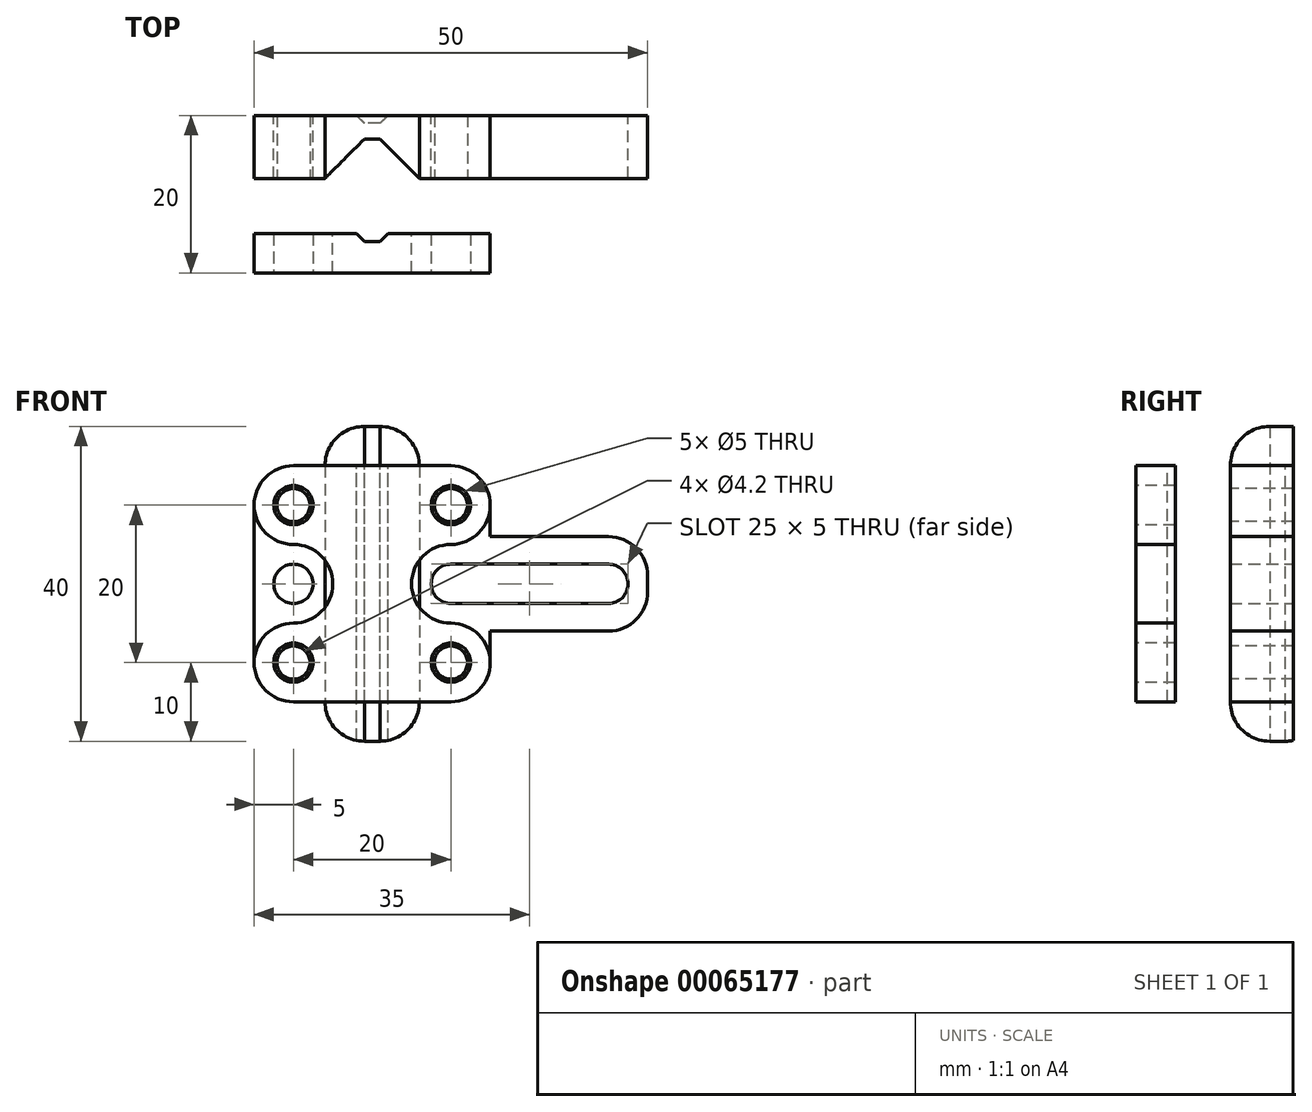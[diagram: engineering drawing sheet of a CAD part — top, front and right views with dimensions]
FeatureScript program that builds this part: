
annotation { "Feature Type Name" : "Feature", "Feature Type Description" : "" }
export const myFeature = defineFeature(function(context is Context, id is Id, definition is map)
    precondition{}
    {
        {
            var Q0;
            Q0=qCreatedBy(makeId("Front.planeOp"),FACE);
            var sketch = newSketch(context, id + "F0", { "sketchPlane" : qUnion([Q0])});
            skCircle(sketch, "E0", {"center": v(0, 0) * mm, "radius": 2.5 * mm, "construction": true});
            skCircle(sketch, "E1.0.1.0", {"center": v(0, 10) * mm, "radius": 2.5 * mm, "construction": true});
            skCircle(sketch, "E1.0.2.0", {"center": v(0, 20) * mm, "radius": 2.5 * mm, "construction": true});
            skCircle(sketch, "E1.0.3.0", {"center": v(0, 30) * mm, "radius": 2.5 * mm, "construction": true});
            skCircle(sketch, "E1.0.4.0", {"center": v(0, 40) * mm, "radius": 2.5 * mm, "construction": true});
            skCircle(sketch, "E1.1.0.0", {"center": v(10, 0) * mm, "radius": 2.5 * mm, "construction": true});
            skCircle(sketch, "E1.1.1.0", {"center": v(10, 10) * mm, "radius": 2.5 * mm, "construction": true});
            skCircle(sketch, "E1.1.2.0", {"center": v(10, 20) * mm, "radius": 2.5 * mm, "construction": true});
            skCircle(sketch, "E1.1.3.0", {"center": v(10, 30) * mm, "radius": 2.5 * mm, "construction": true});
            skCircle(sketch, "E1.1.4.0", {"center": v(10, 40) * mm, "radius": 2.5 * mm, "construction": true});
            skCircle(sketch, "E1.2.0.0", {"center": v(20, 0) * mm, "radius": 2.5 * mm, "construction": true});
            skCircle(sketch, "E1.2.1.0", {"center": v(20, 10) * mm, "radius": 2.1 * mm, "construction": true});
            skCircle(sketch, "E1.2.2.0", {"center": v(20, 20) * mm, "radius": 2.5 * mm});
            skCircle(sketch, "E1.2.3.0", {"center": v(20, 30) * mm, "radius": 2.1 * mm, "construction": true});
            skCircle(sketch, "E1.2.4.0", {"center": v(20, 40) * mm, "radius": 2.5 * mm, "construction": true});
            skCircle(sketch, "E1.3.0.0", {"center": v(30, 0) * mm, "radius": 2.5 * mm, "construction": true});
            skCircle(sketch, "E1.3.1.0", {"center": v(30, 10) * mm, "radius": 2.5 * mm, "construction": true});
            skCircle(sketch, "E1.3.2.0", {"center": v(30, 20) * mm, "radius": 2.5 * mm, "construction": true});
            skCircle(sketch, "E1.3.3.0", {"center": v(30, 30) * mm, "radius": 2.5 * mm, "construction": true});
            skCircle(sketch, "E1.3.4.0", {"center": v(30, 40) * mm, "radius": 2.5 * mm, "construction": true});
            skCircle(sketch, "E1.4.0.0", {"center": v(40, 0) * mm, "radius": 2.5 * mm, "construction": true});
            skCircle(sketch, "E1.4.1.0", {"center": v(40, 10) * mm, "radius": 2.1 * mm, "construction": true});
            skArc(sketch, "E1.4.2.0", {"start": v(40, 22.5) * mm, "mid": v(37.5, 20) * mm, "end": v(40, 17.5) * mm});
            skCircle(sketch, "E1.4.3.0", {"center": v(40, 30) * mm, "radius": 2.1 * mm, "construction": true});
            skCircle(sketch, "E1.4.4.0", {"center": v(40, 40) * mm, "radius": 2.5 * mm, "construction": true});
            skCircle(sketch, "E1.5.0.0", {"center": v(50, 0) * mm, "radius": 2.5 * mm, "construction": true});
            skCircle(sketch, "E1.5.1.0", {"center": v(50, 10) * mm, "radius": 2.5 * mm, "construction": true});
            skCircle(sketch, "E1.5.3.0", {"center": v(50, 30) * mm, "radius": 2.5 * mm, "construction": true});
            skCircle(sketch, "E1.5.4.0", {"center": v(50, 40) * mm, "radius": 2.5 * mm, "construction": true});
            skCircle(sketch, "E1.6.0.0", {"center": v(60, 0) * mm, "radius": 2.5 * mm, "construction": true});
            skCircle(sketch, "E1.6.1.0", {"center": v(60, 10) * mm, "radius": 2.5 * mm, "construction": true});
            skArc(sketch, "E1.6.2.0", {"start": v(60, 17.5) * mm, "mid": v(62.5, 20) * mm, "end": v(60, 22.5) * mm});
            skCircle(sketch, "E1.6.3.0", {"center": v(60, 30) * mm, "radius": 2.5 * mm, "construction": true});
            skCircle(sketch, "E1.6.4.0", {"center": v(60, 40) * mm, "radius": 2.5 * mm, "construction": true});
            skCircle(sketch, "E1.7.0.0", {"center": v(70, 0) * mm, "radius": 2.5 * mm, "construction": true});
            skCircle(sketch, "E1.7.1.0", {"center": v(70, 10) * mm, "radius": 2.5 * mm, "construction": true});
            skCircle(sketch, "E1.7.2.0", {"center": v(70, 20) * mm, "radius": 2.5 * mm, "construction": true});
            skCircle(sketch, "E1.7.3.0", {"center": v(70, 30) * mm, "radius": 2.5 * mm, "construction": true});
            skCircle(sketch, "E1.7.4.0", {"center": v(70, 40) * mm, "radius": 2.5 * mm, "construction": true});
            skCircle(sketch, "E1.8.0.0", {"center": v(80, 0) * mm, "radius": 2.5 * mm, "construction": true});
            skCircle(sketch, "E1.8.1.0", {"center": v(80, 10) * mm, "radius": 2.5 * mm, "construction": true});
            skCircle(sketch, "E1.8.2.0", {"center": v(80, 20) * mm, "radius": 2.5 * mm, "construction": true});
            skCircle(sketch, "E1.8.3.0", {"center": v(80, 30) * mm, "radius": 2.5 * mm, "construction": true});
            skCircle(sketch, "E1.8.4.0", {"center": v(80, 40) * mm, "radius": 2.5 * mm, "construction": true});
            skLineSegment(sketch, "E1.direction1", {"start": v(0, 0) * mm, "end": v(10, 0) * mm, "construction": true});
            skLineSegment(sketch, "E1.direction2", {"start": v(0, 0) * mm, "end": v(0, 10) * mm, "construction": true});
            skLineSegment(sketch, "E2.bottom", {"start": v(36, 0) * mm, "end": v(24, 0) * mm});
            skLineSegment(sketch, "E2.top", {"start": v(36, 40) * mm, "end": v(24, 40) * mm});
            skLineSegment(sketch, "E2.left", {"start": v(36, 0) * mm, "end": v(36, 5) * mm});
            skLineSegment(sketch, "E2.right", {"start": v(24, 0) * mm, "end": v(24, 5) * mm});
            skLineSegment(sketch, "E3.bottom", {"start": v(65, 14) * mm, "end": v(45, 14) * mm});
            skLineSegment(sketch, "E3.top", {"start": v(65, 26) * mm, "end": v(45, 26) * mm});
            skLineSegment(sketch, "E3.left", {"start": v(65, 14) * mm, "end": v(65, 26) * mm});
            skLineSegment(sketch, "E3.right", {"start": v(15, 14) * mm, "end": v(15, 26) * mm});
            skLineSegment(sketch, "E4.trimOffspring", {"start": v(24, 35) * mm, "end": v(24, 40) * mm});
            skLineSegment(sketch, "E5.trimOffspring", {"start": v(36, 35) * mm, "end": v(36, 40) * mm});
            skLineSegment(sketch, "E6", {"start": v(40, 22.5) * mm, "end": v(60, 22.5) * mm});
            skLineSegment(sketch, "E7", {"start": v(60, 17.5) * mm, "end": v(40, 17.5) * mm});
            skLineSegment(sketch, "E8", {"start": v(15, 26) * mm, "end": v(15, 35) * mm});
            skLineSegment(sketch, "E9", {"start": v(15, 35) * mm, "end": v(24, 35) * mm});
            skLineSegment(sketch, "E10", {"start": v(45, 35) * mm, "end": v(45, 26) * mm});
            skLineSegment(sketch, "E11", {"start": v(45, 5) * mm, "end": v(36, 5) * mm});
            skLineSegment(sketch, "E12", {"start": v(15, 5) * mm, "end": v(15, 14) * mm});
            skLineSegment(sketch, "E13.trimOffspring", {"start": v(36, 35) * mm, "end": v(45, 35) * mm});
            skLineSegment(sketch, "E14.trimOffspring", {"start": v(24, 5) * mm, "end": v(15, 5) * mm});
            skLineSegment(sketch, "E15.trimOffspring", {"start": v(45, 14) * mm, "end": v(45, 5) * mm});
            skSolve(sketch);
        }
        {
            var Q0;
            Q0=makeQuery(id+"F0.imprint","IMPRINT",FACE,{"disambiguationData":[TD([[makeQuery(id+"F0.imprint","IMPRINT",EDGE,{"derivedFrom":sQuery(id+"F0.wireOp",EDGE,"E1.2.1.0")}),-1.0]])]});
            var Q1;
            Q1=makeQuery(id+"F0.imprint","IMPRINT",FACE,{"disambiguationData":[TD([[makeQuery(id+"F0.imprint","IMPRINT",EDGE,{"derivedFrom":sQuery(id+"F0.wireOp",EDGE,"E1.2.2.0")}),-1.0]])]});
            extrude(context, id + "F1", {"entities" : qUnion([Q0, Q1]), "depth" : 8 * mm});
        }
        {
            var Q0;
            Q0=qCreatedBy(makeId("Top.planeOp"),FACE);
            var sketch = newSketch(context, id + "F2", { "sketchPlane" : qUnion([Q0])});
            skLineSegment(sketch, "E16", {"start": v(24, -8) * mm, "end": v(29, -3) * mm});
            skLineSegment(sketch, "E17", {"start": v(29, -3) * mm, "end": v(31, -3) * mm});
            skLineSegment(sketch, "E18", {"start": v(31, -3) * mm, "end": v(36, -8) * mm});
            skLineSegment(sketch, "E19", {"start": v(36, -8) * mm, "end": v(24, -8) * mm});
            skSolve(sketch);
        }
        {
            var Q0;
            Q0=makeQuery(id+"F2.imprint","IMPRINT",FACE,{"disambiguationData":[TD([[makeQuery(id+"F2.imprint","IMPRINT",EDGE,{"derivedFrom":sQuery(id+"F2.wireOp",EDGE,"E16")}),-1.0]])]});
            extrude(context, id + "F3", {"entities" : qUnion([Q0]), "operationType" : NewBodyOperationType.REMOVE, "depth" : 40 * mm});
        }
        {
            var Q0;
            Q0=sQuery(id+"F0.wireOp",VERTEX,"E1.2.3.0.center");
            var Q1;
            Q1=sQuery(id+"F0.wireOp",VERTEX,"E1.4.3.0.center");
            var Q2;
            Q2=sQuery(id+"F0.wireOp",VERTEX,"E1.4.1.0.center");
            var Q3;
            Q3=sQuery(id+"F0.wireOp",VERTEX,"E1.2.1.0.center");
            var Q4;
            Q4=makeQuery(id+"F1.opExtrude","SWEPT_BODY",BODY,{"disambiguationData":[OSD([sQuery(id+"F0.wireOp",EDGE,"E1.2.1.0"),sQuery(id+"F0.wireOp",EDGE,"E1.2.2.0"),sQuery(id+"F0.wireOp",EDGE,"E1.2.3.0"),sQuery(id+"F0.wireOp",EDGE,"E1.4.1.0"),sQuery(id+"F0.wireOp",EDGE,"E1.4.2.0"),sQuery(id+"F0.wireOp",EDGE,"E1.4.3.0"),sQuery(id+"F0.wireOp",EDGE,"E1.6.2.0"),sQuery(id+"F0.wireOp",EDGE,"E2.bottom"),sQuery(id+"F0.wireOp",EDGE,"E2.top"),sQuery(id+"F0.wireOp",EDGE,"E2.left"),sQuery(id+"F0.wireOp",EDGE,"E2.right"),sQuery(id+"F0.wireOp",EDGE,"E3.bottom"),sQuery(id+"F0.wireOp",EDGE,"E3.top"),sQuery(id+"F0.wireOp",EDGE,"E3.left"),sQuery(id+"F0.wireOp",EDGE,"E3.right"),sQuery(id+"F0.wireOp",EDGE,"E4.trimOffspring"),sQuery(id+"F0.wireOp",EDGE,"E5.trimOffspring"),sQuery(id+"F0.wireOp",EDGE,"E6"),sQuery(id+"F0.wireOp",EDGE,"E7"),sQuery(id+"F0.wireOp",EDGE,"E8"),sQuery(id+"F0.wireOp",EDGE,"E9"),sQuery(id+"F0.wireOp",EDGE,"E10"),sQuery(id+"F0.wireOp",EDGE,"E11"),sQuery(id+"F0.wireOp",EDGE,"E12"),sQuery(id+"F0.wireOp",EDGE,"E13.trimOffspring"),sQuery(id+"F0.wireOp",EDGE,"E14.trimOffspring"),sQuery(id+"F0.wireOp",EDGE,"E15.trimOffspring")])]});
            hole(context, id + "F4", {"style" : HoleStyle.SIMPLE, "endStyle" : HoleEndStyle.THROUGH, "oppositeDirection" : true, "standardTappedOrClearance" : lookupTablePath({ "standard" : "ISO", "engagement" : "75%", "pitch" : "0.8 mm", "size" : "M5", "type" : "Tapped" }), "standardBlindInLast" : lookupTablePath({ "standard" : "ISO", "engagement" : "75%", "pitch" : "0.8 mm", "size" : "M5", "type" : "Tapped" }), "holeDiameter" : 4.2 * mm, "showTappedDepth" : true, "isTappedThrough" : true, "tappedDepth" : 12 * mm, "tapClearance" : 3, "locations" : qUnion([Q0, Q1, Q2, Q3]), "scope" : qUnion([Q4]), "majorDiameter" : 5 * mm, "startStyle" : HoleStartStyle.PART});
        }
        {
            var Q0;
            Q0=makeQuery(id+"F1.opExtrude","SWEPT_EDGE",EDGE,{"disambiguationData":[OSD([sQuery(id+"F0.wireOp",EDGE,"E2.top"),sQuery(id+"F0.wireOp",EDGE,"E5.trimOffspring")])]});
            var Q1;
            Q1=makeQuery(id+"F1.opExtrude","SWEPT_EDGE",EDGE,{"disambiguationData":[OSD([sQuery(id+"F0.wireOp",EDGE,"E2.top"),sQuery(id+"F0.wireOp",EDGE,"E4.trimOffspring")])]});
            var Q2;
            Q2=makeQuery(id+"F1.opExtrude","SWEPT_EDGE",EDGE,{"disambiguationData":[OSD([sQuery(id+"F0.wireOp",EDGE,"E10"),sQuery(id+"F0.wireOp",EDGE,"E13.trimOffspring")])]});
            var Q3;
            Q3=makeQuery(id+"F1.opExtrude","SWEPT_EDGE",EDGE,{"disambiguationData":[OSD([sQuery(id+"F0.wireOp",EDGE,"E8"),sQuery(id+"F0.wireOp",EDGE,"E9")])]});
            var Q4;
            Q4=makeQuery(id+"F1.opExtrude","SWEPT_EDGE",EDGE,{"disambiguationData":[OSD([sQuery(id+"F0.wireOp",EDGE,"E12"),sQuery(id+"F0.wireOp",EDGE,"E14.trimOffspring")])]});
            var Q5;
            Q5=makeQuery(id+"F1.opExtrude","SWEPT_EDGE",EDGE,{"disambiguationData":[OSD([sQuery(id+"F0.wireOp",EDGE,"E2.bottom"),sQuery(id+"F0.wireOp",EDGE,"E2.left")])]});
            var Q6;
            Q6=makeQuery(id+"F1.opExtrude","SWEPT_EDGE",EDGE,{"disambiguationData":[OSD([sQuery(id+"F0.wireOp",EDGE,"E2.bottom"),sQuery(id+"F0.wireOp",EDGE,"E2.right")])]});
            var Q7;
            Q7=makeQuery(id+"F1.opExtrude","SWEPT_EDGE",EDGE,{"disambiguationData":[OSD([sQuery(id+"F0.wireOp",EDGE,"E11"),sQuery(id+"F0.wireOp",EDGE,"E15.trimOffspring")])]});
            var Q8;
            Q8=makeQuery(id+"F1.opExtrude","SWEPT_EDGE",EDGE,{"disambiguationData":[OSD([sQuery(id+"F0.wireOp",EDGE,"E3.top"),sQuery(id+"F0.wireOp",EDGE,"E3.left")])]});
            var Q9;
            Q9=makeQuery(id+"F1.opExtrude","SWEPT_EDGE",EDGE,{"disambiguationData":[OSD([sQuery(id+"F0.wireOp",EDGE,"E3.bottom"),sQuery(id+"F0.wireOp",EDGE,"E3.left")])]});
            fillet(context, id + "F5", {"entities" : qUnion([Q0, Q1, Q2, Q3, Q4, Q5, Q6, Q7, Q8, Q9]), "radius" : 5 * mm, "tangentPropagation" : true, "allowEdgeOverflow" : false});
        }
        {
            var Q0;
            Q0=qCreatedBy(makeId("Front.planeOp"),FACE);
            var sketch = newSketch(context, id + "F6", { "sketchPlane" : qUnion([Q0])});
            skLineSegment(sketch, "E20.bottom", {"start": v(45, 35) * mm, "end": v(15, 35) * mm});
            skLineSegment(sketch, "E20.top", {"start": v(45, 5) * mm, "end": v(15, 5) * mm});
            skLineSegment(sketch, "E20.left", {"start": v(45, 35) * mm, "end": v(45, 5) * mm});
            skLineSegment(sketch, "E20.right", {"start": v(15, 35) * mm, "end": v(15, 5) * mm});
            skPoint(sketch, "E20.middle", {"position": v(30, 20) * mm});
            skArc(sketch, "E21", {"start": v(40, 25) * mm, "mid": v(35, 20) * mm, "end": v(40, 15) * mm});
            skArc(sketch, "E22", {"start": v(20, 15) * mm, "mid": v(25, 20) * mm, "end": v(20, 25) * mm});
            skLineSegment(sketch, "E23", {"start": v(40, 25) * mm, "end": v(45, 25) * mm});
            skLineSegment(sketch, "E24", {"start": v(40, 15) * mm, "end": v(45, 15) * mm});
            skLineSegment(sketch, "E25", {"start": v(20, 25) * mm, "end": v(15, 25) * mm});
            skLineSegment(sketch, "E26", {"start": v(20, 15) * mm, "end": v(15, 15) * mm});
            skSolve(sketch);
        }
        {
            var Q0;
            {var subQ4=sQuery(id+"F6.wireOp",EDGE,"E20.bottom");Q0=makeQuery(id+"F6.imprint","IMPRINT",FACE,{"disambiguationData":[TD([[makeQuery(id+"F6.imprint","IMPRINT",EDGE,{"derivedFrom":subQ4}),1.0]])]});}
            extrude(context, id + "F7", {"entities" : qUnion([Q0]), "depth" : 5 * mm});
        }
        {
            var Q0;
            Q0=sQuery(id+"F0.wireOp",VERTEX,"E1.4.3.0.center");
            var Q1;
            Q1=sQuery(id+"F0.wireOp",VERTEX,"E1.2.3.0.center");
            var Q2;
            Q2=sQuery(id+"F0.wireOp",VERTEX,"E1.2.1.0.center");
            var Q3;
            Q3=sQuery(id+"F0.wireOp",VERTEX,"E1.4.1.0.center");
            var Q4;
            Q4=makeQuery(id+"F7.opExtrude","SWEPT_BODY",BODY,{"disambiguationData":[OSD([sQuery(id+"F6.wireOp",EDGE,"E20.bottom"),sQuery(id+"F6.wireOp",EDGE,"E20.top"),sQuery(id+"F6.wireOp",EDGE,"E20.left"),sQuery(id+"F6.wireOp",EDGE,"E20.right")])]});
            hole(context, id + "F8", {"style" : HoleStyle.SIMPLE, "endStyle" : HoleEndStyle.THROUGH, "oppositeDirection" : true, "holeDiameter" : 5 * mm, "isTappedThrough" : true, "tappedDepth" : 12 * mm, "tapClearance" : 3, "locations" : qUnion([Q0, Q1, Q2, Q3]), "scope" : qUnion([Q4]), "startStyle" : HoleStartStyle.PART});
        }
        {
            var Q0;
            Q0=makeQuery(id+"F7.opExtrude","SWEPT_EDGE",EDGE,{"disambiguationData":[OSD([sQuery(id+"F6.wireOp",EDGE,"E20.bottom"),sQuery(id+"F6.wireOp",EDGE,"E20.left")])]});
            var Q1;
            Q1=makeQuery(id+"F7.opExtrude","SWEPT_EDGE",EDGE,{"disambiguationData":[OSD([sQuery(id+"F6.wireOp",EDGE,"E20.bottom"),sQuery(id+"F6.wireOp",EDGE,"E20.right")])]});
            var Q2;
            Q2=makeQuery(id+"F7.opExtrude","SWEPT_EDGE",EDGE,{"disambiguationData":[OSD([sQuery(id+"F6.wireOp",EDGE,"E20.top"),sQuery(id+"F6.wireOp",EDGE,"E20.left")])]});
            var Q3;
            Q3=makeQuery(id+"F7.opExtrude","SWEPT_EDGE",EDGE,{"disambiguationData":[OSD([sQuery(id+"F6.wireOp",EDGE,"E20.top"),sQuery(id+"F6.wireOp",EDGE,"E20.right")])]});
            fillet(context, id + "F9", {"entities" : qUnion([Q0, Q1, Q2, Q3]), "radius" : 5 * mm, "tangentPropagation" : true, "allowEdgeOverflow" : false});
        }
        {
            var Q0;
            Q0=makeQuery(id+"F7.opExtrude","SWEPT_FACE",FACE,{"disambiguationData":[OSD([sQuery(id+"F6.wireOp",EDGE,"E20.bottom")])]});
            var sketch = newSketch(context, id + "F10", { "sketchPlane" : qUnion([Q0])});
            skPoint(sketch, "E27.endSnap0", {"position": v(30, 0) * mm});
            skLineSegment(sketch, "E28", {"start": v(28, 0) * mm, "end": v(32, 0) * mm});
            skPoint(sketch, "E29.orphan", {"position": v(30, 2) * mm});
            skPoint(sketch, "E30.orphan", {"position": v(30, -2.5) * mm});
            skLineSegment(sketch, "E31.MirrorCS", {"start": v(29, -1) * mm, "end": v(31, -1) * mm});
            skLineSegment(sketch, "E32.MirrorCS", {"start": v(32, 0) * mm, "end": v(31, -1) * mm});
            skLineSegment(sketch, "E33.MirrorCS", {"start": v(29, -1) * mm, "end": v(28, 0) * mm});
            skPoint(sketch, "E27.end.orphan", {"position": v(31, 1) * mm});
            skPoint(sketch, "E34.start.orphan", {"position": v(29, 1) * mm});
            skSolve(sketch);
        }
        {
            var Q0;
            Q0 = qSketchRegion(id + "F10", true);
            var Q1;
            Q1 = qConstructionFilter(qBodyType(qCreatedBy(id + "F10" ,EDGE), BodyType.WIRE), ConstructionObject.NO);
            extrude(context, id + "F11", {"entities" : qUnion([Q0]), "operationType" : NewBodyOperationType.REMOVE, "surfaceEntities" : qUnion([Q1]), "oppositeDirection" : true, "depth" : 50 * mm});
        }
        {
            var Q0;
            Q0=makeQuery(id+"F7.opExtrude","SWEPT_BODY",BODY,{"disambiguationData":[OSD([sQuery(id+"F6.wireOp",EDGE,"E20.bottom"),sQuery(id+"F6.wireOp",EDGE,"E20.top"),sQuery(id+"F6.wireOp",EDGE,"E20.left"),sQuery(id+"F6.wireOp",EDGE,"E20.right")])]});
            transform(context, id + "F12", {"entities" : qUnion([Q0]), "transformType" : TransformType.TRANSLATION_3D, "dx" : 0 * mm, "dy" : -15 * mm, "dz" : 0 * mm, "makeCopy" : false});
        }
        {
            var Q0;
            Q0=makeQuery(id+"F7.opExtrude","SWEPT_EDGE",EDGE,{"disambiguationData":[OSD([sQuery(id+"F6.wireOp",EDGE,"E20.right"),sQuery(id+"F6.wireOp",EDGE,"E25")])]});
            var Q1;
            Q1=makeQuery(id+"F7.opExtrude","SWEPT_EDGE",EDGE,{"disambiguationData":[OSD([sQuery(id+"F6.wireOp",EDGE,"E20.left"),sQuery(id+"F6.wireOp",EDGE,"E23")])]});
            var Q2;
            Q2=makeQuery(id+"F7.opExtrude","SWEPT_EDGE",EDGE,{"disambiguationData":[OSD([sQuery(id+"F6.wireOp",EDGE,"E20.left"),sQuery(id+"F6.wireOp",EDGE,"E24")])]});
            var Q3;
            Q3=makeQuery(id+"F7.opExtrude","SWEPT_EDGE",EDGE,{"disambiguationData":[OSD([sQuery(id+"F6.wireOp",EDGE,"E20.right"),sQuery(id+"F6.wireOp",EDGE,"E26")])]});
            fillet(context, id + "F13", {"entities" : qUnion([Q0, Q1, Q2, Q3]), "radius" : 5 * mm, "tangentPropagation" : true, "allowEdgeOverflow" : false});
        }
    });
